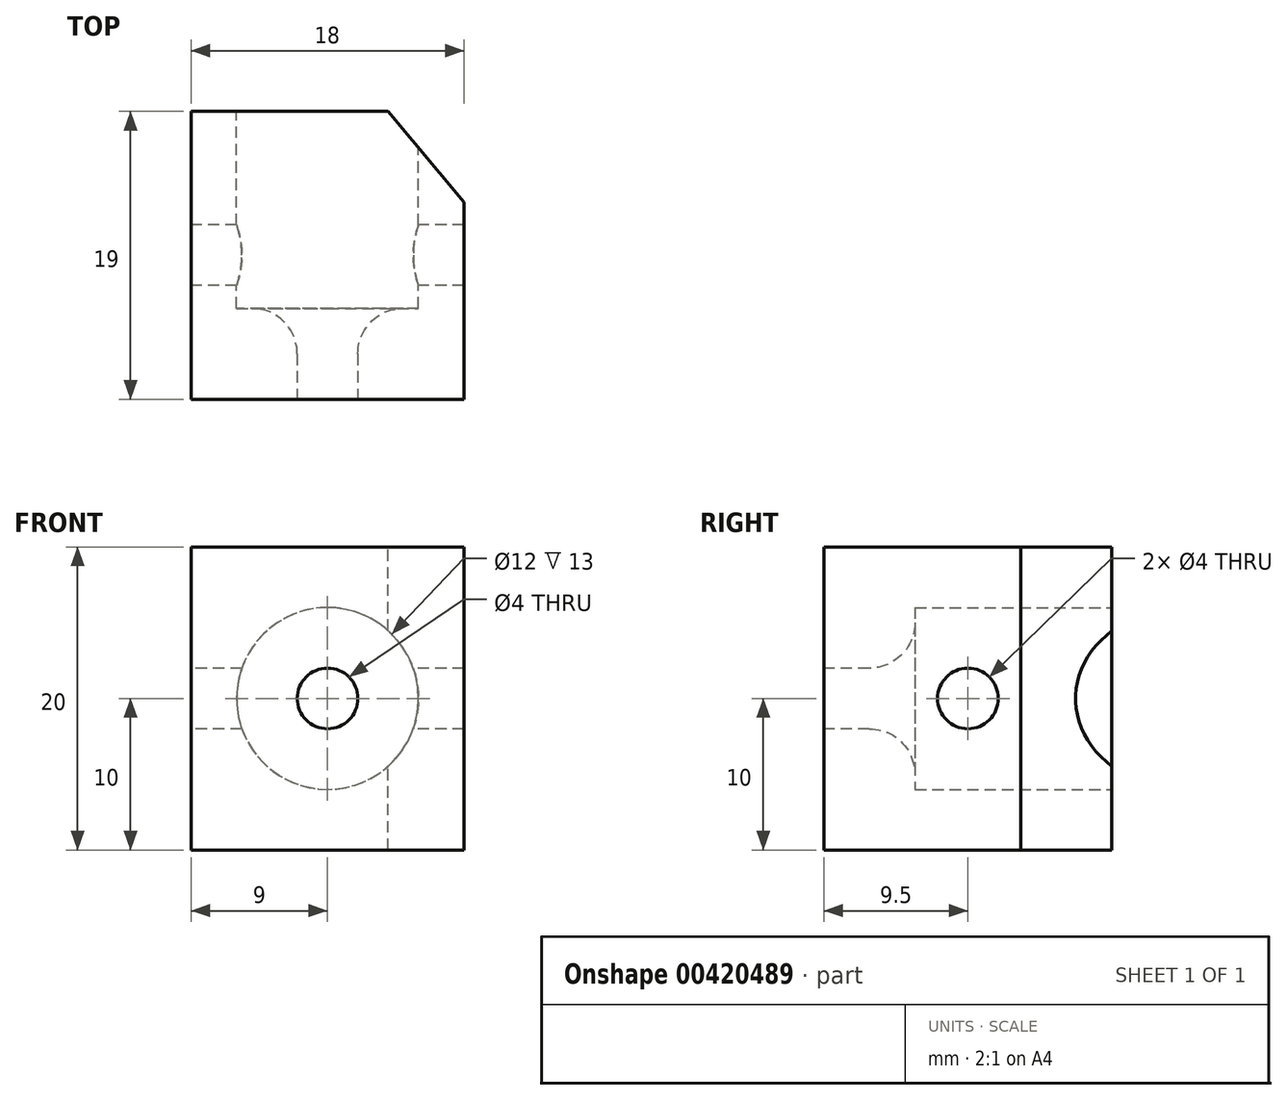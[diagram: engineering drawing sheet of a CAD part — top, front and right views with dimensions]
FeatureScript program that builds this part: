
annotation { "Feature Type Name" : "Feature", "Feature Type Description" : "" }
export const myFeature = defineFeature(function(context is Context, id is Id, definition is map)
    precondition{}
    {
        {
            var Q0;
            Q0=qCreatedBy(makeId("Top.planeOp"),FACE);
            var sketch = newSketch(context, id + "F0", { "sketchPlane" : qUnion([Q0])});
            skLineSegment(sketch, "E0.bottom", {"start": v(9, -9.5) * mm, "end": v(-9, -9.5) * mm});
            skLineSegment(sketch, "E0.top", {"start": v(9, 9.5) * mm, "end": v(-9, 9.5) * mm});
            skLineSegment(sketch, "E0.left", {"start": v(9, -9.5) * mm, "end": v(9, 9.5) * mm});
            skLineSegment(sketch, "E0.right", {"start": v(-9, -9.5) * mm, "end": v(-9, 9.5) * mm});
            skPoint(sketch, "E0.middle", {"position": v(0, 0) * mm});
            skSolve(sketch);
        }
        {
            var Q0;
            Q0=makeQuery(id+"F0.imprint","IMPRINT",FACE,{"disambiguationData":[TD([[makeQuery(id+"F0.imprint","IMPRINT",EDGE,{"derivedFrom":sQuery(id+"F0.wireOp",EDGE,"E0.bottom")}),-1.0]])]});
            extrude(context, id + "F1", {"entities" : qUnion([Q0]), "depth" : 20 * mm});
        }
        {
            var Q0;
            Q0=makeQuery(id+"F1.opExtrude","SWEPT_FACE",FACE,{"disambiguationData":[OSD([sQuery(id+"F0.wireOp",EDGE,"E0.bottom")])]});
            var sketch = newSketch(context, id + "F2", { "sketchPlane" : qUnion([Q0])});
            skLineSegment(sketch, "E1", {"start": v(-9, 10) * mm, "end": v(9, 10) * mm, "construction": true});
            skCircle(sketch, "E2", {"center": v(0, 10) * mm, "radius": 2 * mm});
            skSolve(sketch);
        }
        {
            var Q0;
            Q0=makeQuery(id+"F1.opExtrude","SWEPT_FACE",FACE,{"disambiguationData":[OSD([sQuery(id+"F0.wireOp",EDGE,"E0.top")])]});
            var sketch = newSketch(context, id + "F3", { "sketchPlane" : qUnion([Q0])});
            skLineSegment(sketch, "E3", {"start": v(-9, 10) * mm, "end": v(9, 10) * mm, "construction": true});
            skCircle(sketch, "E4", {"center": v(0, 10) * mm, "radius": 6 * mm});
            skSolve(sketch);
        }
        {
            var Q0;
            Q0=makeQuery(id+"F3.imprint","IMPRINT",FACE,{"disambiguationData":[TD([[makeQuery(id+"F3.imprint","IMPRINT",EDGE,{"derivedFrom":sQuery(id+"F3.wireOp",EDGE,"E4")}),1.0]])]});
            extrude(context, id + "F4", {"entities" : qUnion([Q0]), "operationType" : NewBodyOperationType.REMOVE, "oppositeDirection" : true, "depth" : 13 * mm});
        }
        {
            var Q0;
            Q0=makeQuery(id+"F2.imprint","IMPRINT",FACE,{"disambiguationData":[TD([[makeQuery(id+"F2.imprint","IMPRINT",EDGE,{"derivedFrom":sQuery(id+"F2.wireOp",EDGE,"E2")}),1.0]])]});
            extrude(context, id + "F5", {"entities" : qUnion([Q0]), "operationType" : NewBodyOperationType.REMOVE, "oppositeDirection" : true, "depth" : 18 * mm});
        }
        {
            var Q0;
            Q0=makeQuery(id+"F5.boolean.opBoolean","INTERSECT",EDGE,{"derivedFrom":[makeQuery(id+"F4.boolean.opBoolean","COPY",FACE,{"derivedFrom":makeQuery(id+"F4.opExtrude","CAP_FACE",FACE,{"disambiguationData":[OSD([sQuery(id+"F3.wireOp",EDGE,"E4")])],"isStart":false})}),makeQuery(id+"F5.opExtrude","SWEPT_FACE",FACE,{"disambiguationData":[OSD([sQuery(id+"F2.wireOp",EDGE,"E2")])]})]});
            fillet(context, id + "F6", {"entities" : qUnion([Q0]), "radius" : 3 * mm, "tangentPropagation" : true, "allowEdgeOverflow" : false});
        }
        {
            var Q0;
            Q0=makeQuery(id+"F1.opExtrude","SWEPT_FACE",FACE,{"disambiguationData":[OSD([sQuery(id+"F0.wireOp",EDGE,"E0.right")])]});
            var sketch = newSketch(context, id + "F7", { "sketchPlane" : qUnion([Q0])});
            skLineSegment(sketch, "E5", {"start": v(-9.5, 10) * mm, "end": v(9.5, 10) * mm, "construction": true});
            skCircle(sketch, "E6", {"center": v(0, 10) * mm, "radius": 2 * mm});
            skSolve(sketch);
        }
        {
            var Q0;
            Q0=makeQuery(id+"F7.imprint","IMPRINT",FACE,{"disambiguationData":[TD([[makeQuery(id+"F7.imprint","IMPRINT",EDGE,{"derivedFrom":sQuery(id+"F7.wireOp",EDGE,"E6")}),1.0]])]});
            extrude(context, id + "F8", {"entities" : qUnion([Q0]), "operationType" : NewBodyOperationType.REMOVE, "oppositeDirection" : true, "depth" : 25 * mm});
        }
        {
            var Q0;
            Q0=makeQuery(id+"F1.opExtrude","CAP_FACE",FACE,{"disambiguationData":[OSD([sQuery(id+"F0.wireOp",EDGE,"E0.bottom"),sQuery(id+"F0.wireOp",EDGE,"E0.top"),sQuery(id+"F0.wireOp",EDGE,"E0.left"),sQuery(id+"F0.wireOp",EDGE,"E0.right")])],"isStart":false});
            var sketch = newSketch(context, id + "F9", { "sketchPlane" : qUnion([Q0])});
            skLineSegment(sketch, "E7", {"start": v(9, -9.5) * mm, "end": v(9, 3.5) * mm, "construction": true});
            skLineSegment(sketch, "E8", {"start": v(-9, 9.5) * mm, "end": v(4, 9.5) * mm, "construction": true});
            skLineSegment(sketch, "E9", {"start": v(4, 9.5) * mm, "end": v(9, 3.5) * mm});
            skLineSegment(sketch, "E10", {"start": v(9, 3.5) * mm, "end": v(9, 9.5) * mm});
            skLineSegment(sketch, "E11", {"start": v(9, 9.5) * mm, "end": v(4, 9.5) * mm});
            skSolve(sketch);
        }
        {
            var Q0;
            Q0=makeQuery(id+"F9.imprint","IMPRINT",FACE,{"disambiguationData":[TD([[makeQuery(id+"F9.imprint","IMPRINT",EDGE,{"derivedFrom":sQuery(id+"F9.wireOp",EDGE,"E9")}),1.0]])]});
            extrude(context, id + "F10", {"entities" : qUnion([Q0]), "operationType" : NewBodyOperationType.REMOVE, "oppositeDirection" : true, "depth" : 25 * mm});
        }
    });
